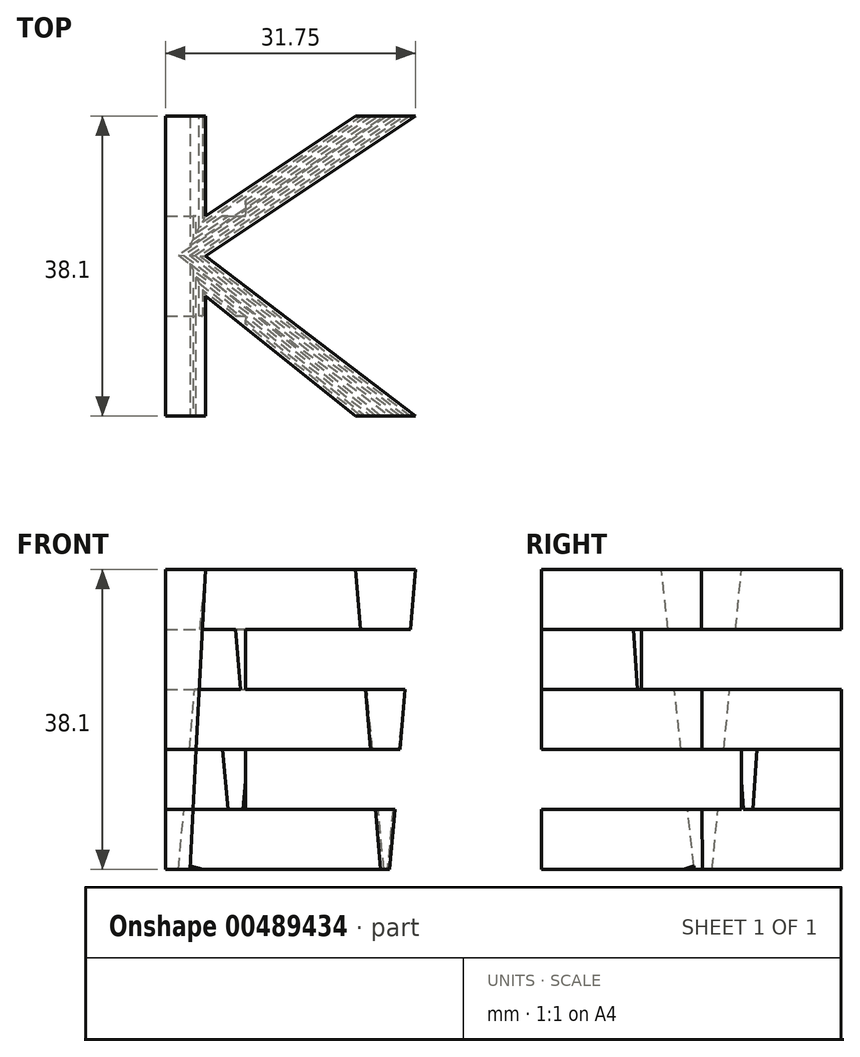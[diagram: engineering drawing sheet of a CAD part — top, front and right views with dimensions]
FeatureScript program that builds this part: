
annotation { "Feature Type Name" : "Feature", "Feature Type Description" : "" }
export const myFeature = defineFeature(function(context is Context, id is Id, definition is map)
    precondition{}
    {
        {
            var Q0;
            Q0=qCreatedBy(makeId("Front.planeOp"),FACE);
            var sketch = newSketch(context, id + "F0", { "sketchPlane" : qUnion([Q0])});
            skLineSegment(sketch, "E0", {"start": v(0, 0) * mm, "end": v(0, 38.1) * mm});
            skLineSegment(sketch, "E1", {"start": v(0, 38.1) * mm, "end": v(38.1, 38.1) * mm});
            skLineSegment(sketch, "E2", {"start": v(38.1, 38.1) * mm, "end": v(38.1, 0) * mm});
            skLineSegment(sketch, "E3", {"start": v(38.1, 0) * mm, "end": v(0, 0) * mm});
            skSolve(sketch);
        }
        {
            var Q0;
            Q0=makeQuery(id+"F0.imprint","IMPRINT",FACE,{"disambiguationData":[TD([[makeQuery(id+"F0.imprint","IMPRINT",EDGE,{"derivedFrom":sQuery(id+"F0.wireOp",EDGE,"E0")}),-1.0]])]});
            extrude(context, id + "F1", {"entities" : qUnion([Q0]), "depth" : 38.1 * mm, "offsetDistance" : 25.4 * mm});
        }
        {
            var Q0;
            Q0=qCreatedBy(makeId("Front.planeOp"),FACE);
            cPlane(context, id + "F2", {"entities" : qUnion([Q0]), "cplaneType" : CPlaneType.OFFSET, "offset" : 38.1 * mm, "width" : 152.4 * mm, "height" : 152.4 * mm});
        }
        {
            var Q0;
            Q0=qCreatedBy(makeId("Right.planeOp"),FACE);
            cPlane(context, id + "F3", {"entities" : qUnion([Q0]), "cplaneType" : CPlaneType.OFFSET, "offset" : 38.1 * mm, "width" : 152.4 * mm, "height" : 152.4 * mm});
        }
        {
            var Q0;
            Q0=qCreatedBy(makeId("Top.planeOp"),FACE);
            cPlane(context, id + "F4", {"entities" : qUnion([Q0]), "cplaneType" : CPlaneType.OFFSET, "offset" : 38.1 * mm, "width" : 152.4 * mm, "height" : 152.4 * mm});
        }
        {
            var Q0;
            Q0=qCreatedBy(id+"F3.planeOp",FACE);
            var sketch = newSketch(context, id + "F5", { "sketchPlane" : qUnion([Q0])});
            skLineSegment(sketch, "E4", {"start": v(0, 0) * mm, "end": v(-38.1, 0) * mm});
            skLineSegment(sketch, "E5", {"start": v(-38.1, 0) * mm, "end": v(-38.1, 38.1) * mm});
            skLineSegment(sketch, "E6", {"start": v(-38.1, 38.1) * mm, "end": v(0, 38.1) * mm});
            skLineSegment(sketch, "E7", {"start": v(0, 38.1) * mm, "end": v(0, 0) * mm});
            skLineSegment(sketch, "E8", {"start": v(0, 30.48) * mm, "end": v(-25.4, 30.48) * mm});
            skLineSegment(sketch, "E9", {"start": v(-25.4, 30.48) * mm, "end": v(-25.4, 22.86) * mm});
            skLineSegment(sketch, "E10", {"start": v(-25.4, 22.86) * mm, "end": v(0, 22.86) * mm});
            skLineSegment(sketch, "E11", {"start": v(-38.1, 15.24) * mm, "end": v(-12.7, 15.24) * mm});
            skLineSegment(sketch, "E12", {"start": v(-12.7, 15.24) * mm, "end": v(-12.7, 7.62) * mm});
            skLineSegment(sketch, "E13", {"start": v(-12.7, 7.62) * mm, "end": v(-38.1, 7.62) * mm});
            skSolve(sketch);
        }
        {
            var Q0;
            {var subQ0=sQuery(id+"F5.wireOp",EDGE,"E8");Q0=makeQuery(id+"F5.imprint","IMPRINT",FACE,{"disambiguationData":[TD([[makeQuery(id+"F5.imprint","IMPRINT",EDGE,{"derivedFrom":subQ0}),1.0]])]});}
            var Q1;
            {var subQ0=sQuery(id+"F5.wireOp",EDGE,"E11");Q1=makeQuery(id+"F5.imprint","IMPRINT",FACE,{"disambiguationData":[TD([[makeQuery(id+"F5.imprint","IMPRINT",EDGE,{"derivedFrom":subQ0}),-1.0]])]});}
            extrude(context, id + "F6", {"entities" : qUnion([Q0, Q1]), "operationType" : NewBodyOperationType.REMOVE, "oppositeDirection" : true, "depth" : 38.1 * mm, "offsetDistance" : 25.4 * mm});
        }
        {
            var Q0;
            Q0=qCreatedBy(id+"F2.planeOp",FACE);
            var sketch = newSketch(context, id + "F7", { "sketchPlane" : qUnion([Q0])});
            skLineSegment(sketch, "E14", {"start": v(0, 0) * mm, "end": v(0, 38.1) * mm});
            skLineSegment(sketch, "E15", {"start": v(0, 38.1) * mm, "end": v(38.1, 38.1) * mm});
            skLineSegment(sketch, "E16", {"start": v(38.1, 38.1) * mm, "end": v(38.1, 0) * mm});
            skLineSegment(sketch, "E17", {"start": v(38.1, 0) * mm, "end": v(0, 0) * mm});
            skLineSegment(sketch, "E18", {"start": v(38.1, 30.48) * mm, "end": v(10.16, 30.48) * mm});
            skLineSegment(sketch, "E19", {"start": v(10.16, 30.48) * mm, "end": v(10.16, 22.86) * mm});
            skLineSegment(sketch, "E20", {"start": v(10.16, 22.86) * mm, "end": v(38.1, 22.86) * mm});
            skLineSegment(sketch, "E21", {"start": v(38.1, 15.24) * mm, "end": v(10.16, 15.24) * mm});
            skLineSegment(sketch, "E22", {"start": v(10.16, 15.24) * mm, "end": v(10.16, 7.62) * mm});
            skLineSegment(sketch, "E23", {"start": v(10.16, 7.62) * mm, "end": v(38.1, 7.62) * mm});
            skLineSegment(sketch, "E24", {"start": v(10.16, 7.62) * mm, "end": v(10.16, 15.24) * mm});
            skLineSegment(sketch, "E25.trimOffspring", {"start": v(10.16, 22.86) * mm, "end": v(10.16, 30.48) * mm});
            skPoint(sketch, "E26.end.orphan", {"position": v(10.16, 0) * mm});
            skSolve(sketch);
        }
        {
            var Q0;
            {var subQ0=sQuery(id+"F7.wireOp",EDGE,"E18");Q0=makeQuery(id+"F7.imprint","IMPRINT",FACE,{"disambiguationData":[TD([[makeQuery(id+"F7.imprint","IMPRINT",EDGE,{"derivedFrom":subQ0}),1.0]])]});}
            var Q1;
            {var subQ0=sQuery(id+"F7.wireOp",EDGE,"E21");Q1=makeQuery(id+"F7.imprint","IMPRINT",FACE,{"disambiguationData":[TD([[makeQuery(id+"F7.imprint","IMPRINT",EDGE,{"derivedFrom":subQ0}),1.0]])]});}
            extrude(context, id + "F8", {"entities" : qUnion([Q0, Q1]), "operationType" : NewBodyOperationType.REMOVE, "oppositeDirection" : true, "depth" : 38.1 * mm, "offsetDistance" : 25.4 * mm});
        }
        {
            var Q0;
            Q0=qCreatedBy(id+"F4.planeOp",FACE);
            var sketch = newSketch(context, id + "F9", { "sketchPlane" : qUnion([Q0])});
            skLineSegment(sketch, "E27", {"start": v(0, 0) * mm, "end": v(0, -38.1) * mm});
            skLineSegment(sketch, "E28", {"start": v(0, -38.1) * mm, "end": v(38.1, -38.1) * mm});
            skLineSegment(sketch, "E29", {"start": v(38.1, -38.1) * mm, "end": v(38.1, 0) * mm});
            skLineSegment(sketch, "E30", {"start": v(38.1, 0) * mm, "end": v(0, 0) * mm});
            skLineSegment(sketch, "E31", {"start": v(5.08, 0) * mm, "end": v(5.08, -12.7) * mm});
            skLineSegment(sketch, "E32", {"start": v(5.08, -12.7) * mm, "end": v(24.13, 0) * mm});
            skLineSegment(sketch, "E33", {"start": v(24.13, 0) * mm, "end": v(31.75, 0) * mm});
            skLineSegment(sketch, "E34", {"start": v(5.08, -17.78) * mm, "end": v(31.75, -38.1) * mm});
            skLineSegment(sketch, "E35", {"start": v(31.75, -38.1) * mm, "end": v(24.13, -38.1) * mm});
            skLineSegment(sketch, "E36", {"start": v(24.13, -38.1) * mm, "end": v(5.08, -22.86) * mm});
            skLineSegment(sketch, "E37", {"start": v(5.08, -22.86) * mm, "end": v(5.08, -38.1) * mm});
            skLineSegment(sketch, "E38", {"start": v(31.75, 0) * mm, "end": v(5.08, -17.78) * mm});
            skSolve(sketch);
        }
        {
            var Q0;
            {var subQ0=sQuery(id+"F9.wireOp",EDGE,"E36");Q0=makeQuery(id+"F9.imprint","IMPRINT",FACE,{"disambiguationData":[TD([[makeQuery(id+"F9.imprint","IMPRINT",EDGE,{"derivedFrom":subQ0}),1.0]])]});}
            var Q1;
            {var subQ2=sQuery(id+"F9.wireOp",EDGE,"E29");Q1=makeQuery(id+"F9.imprint","IMPRINT",FACE,{"disambiguationData":[TD([[makeQuery(id+"F9.imprint","IMPRINT",EDGE,{"derivedFrom":subQ2}),1.0]])]});}
            var Q2;
            {var subQ0=sQuery(id+"F9.wireOp",EDGE,"E31");Q2=makeQuery(id+"F9.imprint","IMPRINT",FACE,{"disambiguationData":[TD([[makeQuery(id+"F9.imprint","IMPRINT",EDGE,{"derivedFrom":subQ0}),1.0]])]});}
            extrude(context, id + "F10", {"entities" : qUnion([Q0, Q1, Q2]), "operationType" : NewBodyOperationType.REMOVE, "oppositeDirection" : true, "depth" : 38.1 * mm, "offsetDistance" : 25.4 * mm, "hasDraft" : true, "draftAngle" : 3 * degree});
        }
    });
